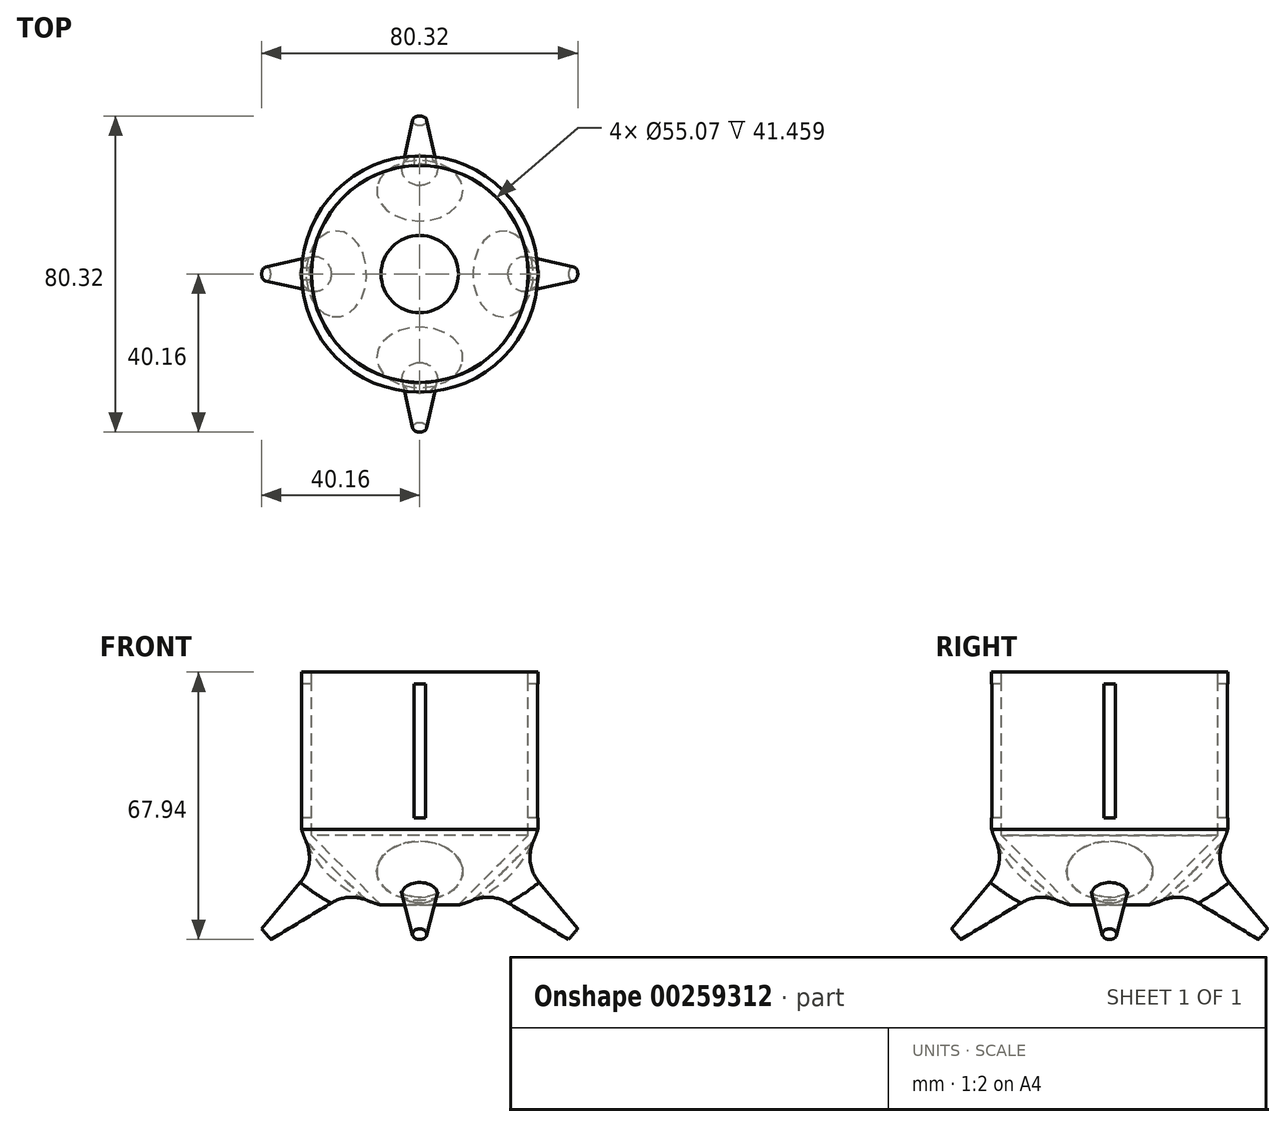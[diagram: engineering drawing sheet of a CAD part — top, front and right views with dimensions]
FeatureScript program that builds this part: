
annotation { "Feature Type Name" : "Feature", "Feature Type Description" : "" }
export const myFeature = defineFeature(function(context is Context, id is Id, definition is map)
    precondition{}
    {
        {
            var Q0;
            Q0=qCreatedBy(makeId("Front.planeOp"),FACE);
            var sketch = newSketch(context, id + "F0", { "sketchPlane" : qUnion([Q0])});
            skLineSegment(sketch, "E0", {"start": v(0, 25.7) * mm, "end": v(0, -34.3) * mm});
            skLineSegment(sketch, "E1", {"start": v(0, 25.7) * mm, "end": v(-30, 25.7) * mm});
            skLineSegment(sketch, "E2", {"start": v(-30, 25.7) * mm, "end": v(-30, -14.3) * mm});
            skArc(sketch, "E3", {"start": v(-30, -14.3) * mm, "mid": v(-18.51, -29.56) * mm, "end": v(0, -34.3) * mm});
            skSolve(sketch);
        }
        {
            var Q0;
            Q0=makeQuery(id+"F0.imprint","IMPRINT",FACE,{"disambiguationData":[TD([[makeQuery(id+"F0.imprint","IMPRINT",EDGE,{"derivedFrom":sQuery(id+"F0.wireOp",EDGE,"E0")}),-1.0]])]});
            var Q1;
            Q1=sQuery(id+"F0.wireOp",EDGE,"E0");
            revolve(context, id + "F1", {"entities" : qUnion([Q0]), "axis" : qUnion([Q1]), "revolveType" : RevolveType.FULL});
        }
        {
            var Q0;
            Q0=qCreatedBy(makeId("Front.planeOp"),FACE);
            var sketch = newSketch(context, id + "F2", { "sketchPlane" : qUnion([Q0])});
            skLineSegment(sketch, "E4", {"start": v(-17.6, -22.48) * mm, "end": v(-38.98, -40.87) * mm});
            skLineSegment(sketch, "E5", {"start": v(-38.98, -40.87) * mm, "end": v(-37.8, -42.24) * mm});
            skLineSegment(sketch, "E6", {"start": v(-37.8, -42.24) * mm, "end": v(-14.3, -27.98) * mm});
            skLineSegment(sketch, "E7", {"start": v(-14.3, -27.98) * mm, "end": v(-19.44, -24.06) * mm});
            skSolve(sketch);
        }
        {
            var Q0;
            Q0 = qSketchRegion(id + "F2", true);
            var Q1;
            Q1=sQuery(id+"F2.wireOp",EDGE,"E4");
            revolve(context, id + "F3", {"operationType" : NewBodyOperationType.ADD, "entities" : qUnion([Q0]), "axis" : qUnion([Q1]), "revolveType" : RevolveType.FULL});
        }
        {
            var Q0;
            Q0=makeQuery(id+"F1.opRevolve","SWEPT_BODY",BODY,{"disambiguationData":[OSD([sQuery(id+"F0.wireOp",EDGE,"E0"),sQuery(id+"F0.wireOp",EDGE,"E1"),sQuery(id+"F0.wireOp",EDGE,"E2"),sQuery(id+"F0.wireOp",EDGE,"E3")])]});
            var Q1;
            Q1=makeQuery(id+"F1.opRevolve","SWEPT_EDGE",EDGE,{"disambiguationData":[OSD([sQuery(id+"F0.wireOp",EDGE,"E1"),sQuery(id+"F0.wireOp",EDGE,"E2")])]});
            circularPattern(context, id + "F4", {"entities" : qUnion([Q0]), "axis" : qUnion([Q1]), "angle" : 360 * degree, "instanceCount" : 4, "equalSpace" : true});
        }
        {
            var Q0;
            Q0=qCreatedBy(makeId("Front.planeOp"),FACE);
            var sketch = newSketch(context, id + "F5", { "sketchPlane" : qUnion([Q0])});
            skLineSegment(sketch, "E8", {"start": v(0, 25.7) * mm, "end": v(-27.53, 25.7) * mm});
            skLineSegment(sketch, "E9", {"start": v(-27.53, 25.7) * mm, "end": v(-27.53, -15.75) * mm});
            skLineSegment(sketch, "E10", {"start": v(-27.53, -15.75) * mm, "end": v(-4.62, -38.67) * mm});
            skLineSegment(sketch, "E11", {"start": v(-4.62, -38.67) * mm, "end": v(0, -38.67) * mm});
            skLineSegment(sketch, "E12", {"start": v(0, -38.67) * mm, "end": v(0, 25.7) * mm});
            skSolve(sketch);
        }
        {
            var Q0;
            Q0 = qSketchRegion(id + "F5", true);
            var Q1;
            Q1=sQuery(id+"F5.wireOp",EDGE,"E12");
            revolve(context, id + "F6", {"operationType" : NewBodyOperationType.REMOVE, "entities" : qUnion([Q0]), "axis" : qUnion([Q1]), "revolveType" : RevolveType.FULL, "oppositeDirection" : true});
        }
        {
            var Q0;
            Q0=qCreatedBy(makeId("Front.planeOp"),FACE);
            var sketch = newSketch(context, id + "F7", { "sketchPlane" : qUnion([Q0])});
            skLineSegment(sketch, "E13", {"start": v(0, 25.7) * mm, "end": v(0, -14.3) * mm});
            skLineSegment(sketch, "E14.bottom", {"start": v(1.5, -11.3) * mm, "end": v(-1.5, -11.3) * mm});
            skLineSegment(sketch, "E14.top", {"start": v(1.5, 22.7) * mm, "end": v(-1.5, 22.7) * mm});
            skLineSegment(sketch, "E14.left", {"start": v(1.5, -11.3) * mm, "end": v(1.5, 22.7) * mm});
            skLineSegment(sketch, "E14.right", {"start": v(-1.5, -11.3) * mm, "end": v(-1.5, 22.7) * mm});
            skPoint(sketch, "E14.middle", {"position": v(0, 5.7) * mm});
            skSolve(sketch);
        }
        {
            var Q0;
            Q0 = qSketchRegion(id + "F7", true);
            extrude(context, id + "F8", {"entities" : qUnion([Q0]), "operationType" : NewBodyOperationType.REMOVE, "endBound" : BoundingType.THROUGH_ALL, "oppositeDirection" : true, "depth" : 25 * mm, "hasSecondDirection" : true, "secondDirectionBound" : SecondDirectionBoundingType.THROUGH_ALL, "secondDirectionOppositeDirection" : false, "secondDirectionDepth" : 25 * mm});
        }
        {
            var Q0;
            Q0=qCreatedBy(makeId("Right.planeOp"),FACE);
            var sketch = newSketch(context, id + "F9", { "sketchPlane" : qUnion([Q0])});
            skLineSegment(sketch, "E15", {"start": v(0, 25.7) * mm, "end": v(0, -14.3) * mm});
            skLineSegment(sketch, "E16.bottom", {"start": v(1.5, -11.3) * mm, "end": v(-1.5, -11.3) * mm});
            skLineSegment(sketch, "E16.top", {"start": v(1.5, 22.7) * mm, "end": v(-1.5, 22.7) * mm});
            skLineSegment(sketch, "E16.left", {"start": v(1.5, -11.3) * mm, "end": v(1.5, 22.7) * mm});
            skLineSegment(sketch, "E16.right", {"start": v(-1.5, -11.3) * mm, "end": v(-1.5, 22.7) * mm});
            skPoint(sketch, "E16.middle", {"position": v(0, 5.7) * mm});
            skSolve(sketch);
        }
        {
            var Q0;
            Q0 = qSketchRegion(id + "F9", true);
            extrude(context, id + "F10", {"entities" : qUnion([Q0]), "operationType" : NewBodyOperationType.REMOVE, "endBound" : BoundingType.THROUGH_ALL, "depth" : 25 * mm, "hasSecondDirection" : true, "secondDirectionBound" : SecondDirectionBoundingType.THROUGH_ALL, "secondDirectionOppositeDirection" : true, "secondDirectionDepth" : 25 * mm});
        }
        {
            var Q0;
            Q0=makeQuery(id+"F3.boolean.opBoolean","INTERSECT",EDGE,{"derivedFrom":[makeQuery(id+"F1.opRevolve","SWEPT_FACE",FACE,{"disambiguationData":[OSD([sQuery(id+"F0.wireOp",EDGE,"E3")])]}),makeQuery(id+"F3.opRevolve","SWEPT_FACE",FACE,{"disambiguationData":[OSD([sQuery(id+"F2.wireOp",EDGE,"E6")])]})]});
            var Q1;
            Q1=makeQuery(id+"F4.opPattern","COPY",EDGE,{"derivedFrom":makeQuery(id+"F3.boolean.opBoolean","INTERSECT",EDGE,{"derivedFrom":[makeQuery(id+"F1.opRevolve","SWEPT_FACE",FACE,{"disambiguationData":[OSD([sQuery(id+"F0.wireOp",EDGE,"E3")])]}),makeQuery(id+"F3.opRevolve","SWEPT_FACE",FACE,{"disambiguationData":[OSD([sQuery(id+"F2.wireOp",EDGE,"E6")])]})]}),"instanceName":"1"});
            var Q2;
            Q2=makeQuery(id+"F4.opPattern","COPY",EDGE,{"derivedFrom":makeQuery(id+"F3.boolean.opBoolean","INTERSECT",EDGE,{"derivedFrom":[makeQuery(id+"F1.opRevolve","SWEPT_FACE",FACE,{"disambiguationData":[OSD([sQuery(id+"F0.wireOp",EDGE,"E3")])]}),makeQuery(id+"F3.opRevolve","SWEPT_FACE",FACE,{"disambiguationData":[OSD([sQuery(id+"F2.wireOp",EDGE,"E6")])]})]}),"instanceName":"2"});
            var Q3;
            Q3=makeQuery(id+"F4.opPattern","COPY",EDGE,{"derivedFrom":makeQuery(id+"F3.boolean.opBoolean","INTERSECT",EDGE,{"derivedFrom":[makeQuery(id+"F1.opRevolve","SWEPT_FACE",FACE,{"disambiguationData":[OSD([sQuery(id+"F0.wireOp",EDGE,"E3")])]}),makeQuery(id+"F3.opRevolve","SWEPT_FACE",FACE,{"disambiguationData":[OSD([sQuery(id+"F2.wireOp",EDGE,"E6")])]})]}),"instanceName":"3"});
            fillet(context, id + "F11", {"entities" : qUnion([Q0, Q1, Q2, Q3]), "radius" : 10 * mm, "tangentPropagation" : true, "allowEdgeOverflow" : false});
        }
    });
